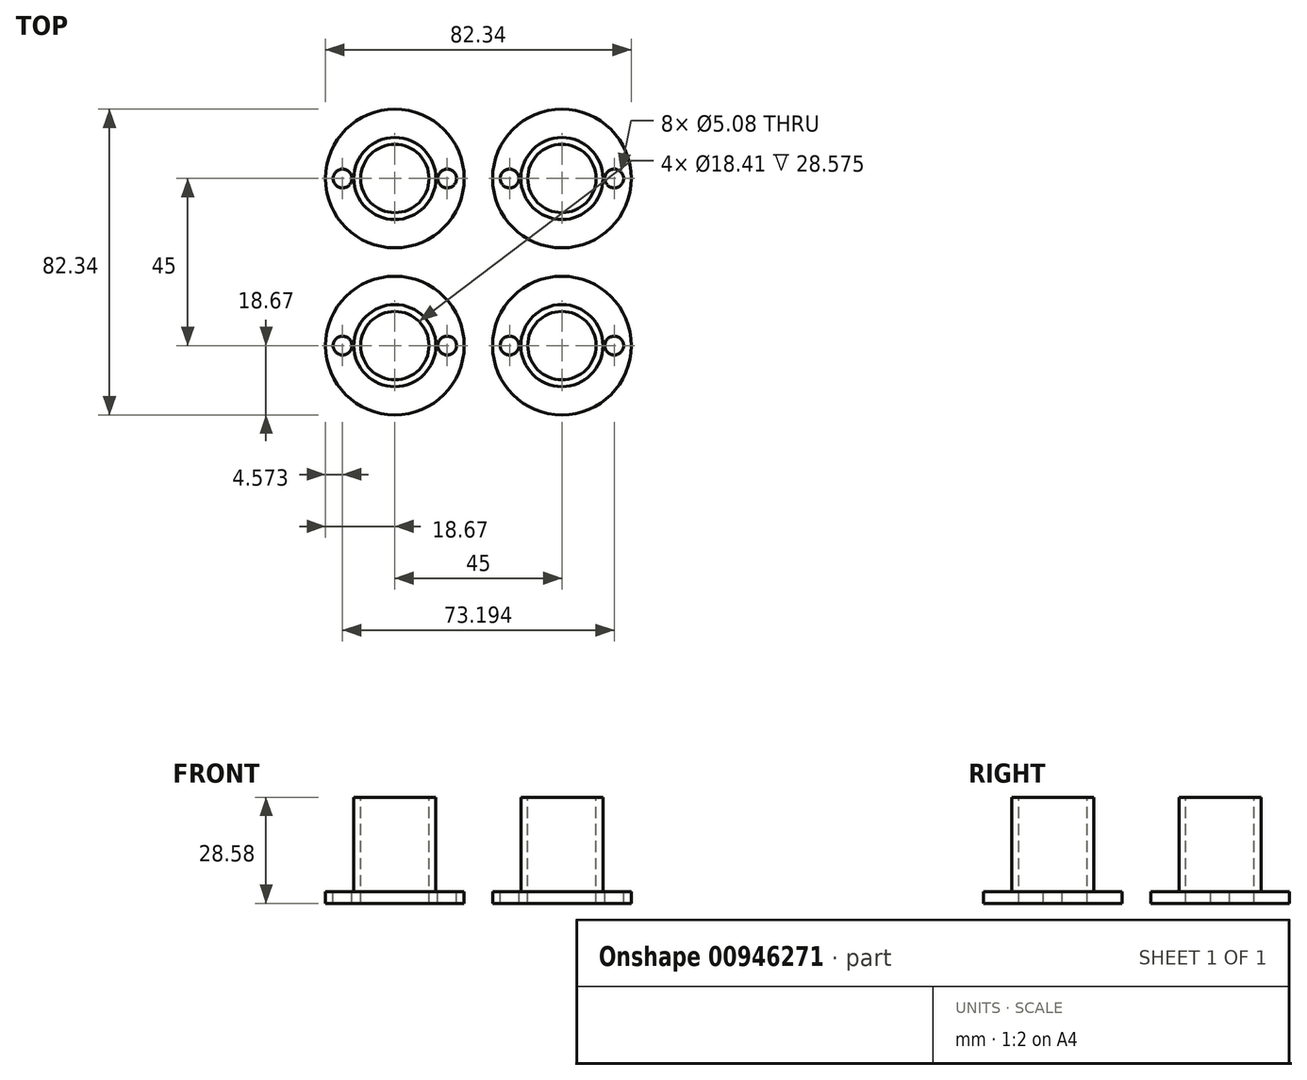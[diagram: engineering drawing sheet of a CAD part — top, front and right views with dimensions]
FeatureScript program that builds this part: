
annotation { "Feature Type Name" : "Feature", "Feature Type Description" : "" }
export const myFeature = defineFeature(function(context is Context, id is Id, definition is map)
    precondition{}
    {
        {
            var Q0;
            Q0=qCreatedBy(makeId("Top.planeOp"),FACE);
            var sketch = newSketch(context, id + "F0", { "sketchPlane" : qUnion([Q0])});
            skCircle(sketch, "E0", {"center": v(0, 0) * mm, "radius": 9.2 * mm});
            skCircle(sketch, "E1.0", {"center": v(0, 0) * mm, "radius": 11.05 * mm});
            skCircle(sketch, "E2.0", {"center": v(0, 0) * mm, "radius": 18.67 * mm});
            skCircle(sketch, "E3.0", {"center": v(0, 0) * mm, "radius": 14.1 * mm});
            skCircle(sketch, "E4", {"center": v(-14.1, 0) * mm, "radius": 2.54 * mm});
            skCircle(sketch, "E5", {"center": v(14.1, 0) * mm, "radius": 2.54 * mm});
            skSolve(sketch);
        }
        {
            var Q0;
            Q0=makeQuery(id+"F0.imprint","IMPRINT",FACE,{"disambiguationData":[TD([[makeQuery(id+"F0.imprint","IMPRINT",EDGE,{"derivedFrom":sQuery(id+"F0.wireOp",EDGE,"E2.0")}),1.0]])]});
            var Q1;
            Q1=makeQuery(id+"F0.imprint","IMPRINT",FACE,{"disambiguationData":[TD([[makeQuery(id+"F0.imprint","IMPRINT",EDGE,{"derivedFrom":sQuery(id+"F0.wireOp",EDGE,"E1.0")}),-1.0]])]});
            var Q2;
            Q2=makeQuery(id+"F0.imprint","IMPRINT",FACE,{"disambiguationData":[TD([[makeQuery(id+"F0.imprint","IMPRINT",EDGE,{"derivedFrom":sQuery(id+"F0.wireOp",EDGE,"E0")}),-1.0]])]});
            extrude(context, id + "F1", {"entities" : qUnion([Q0, Q1, Q2]), "oppositeDirection" : true, "depth" : 3.17 * mm, "offsetDistance" : 25.4 * mm});
        }
        {
            var Q0;
            Q0=makeQuery(id+"F0.imprint","IMPRINT",FACE,{"disambiguationData":[TD([[makeQuery(id+"F0.imprint","IMPRINT",EDGE,{"derivedFrom":sQuery(id+"F0.wireOp",EDGE,"E0")}),-1.0]])]});
            extrude(context, id + "F2", {"entities" : qUnion([Q0]), "operationType" : NewBodyOperationType.ADD, "depth" : 25.4 * mm, "offsetDistance" : 25.4 * mm});
        }
        {
            var Q0;
            Q0=makeQuery(id+"F1.opExtrude","SWEPT_BODY",BODY,{"disambiguationData":[OSD([sQuery(id+"F0.wireOp",EDGE,"E0"),sQuery(id+"F0.wireOp",EDGE,"E2.0"),sQuery(id+"F0.wireOp",EDGE,"E4"),sQuery(id+"F0.wireOp",EDGE,"E5")])]});
            transform(context, id + "F3", {"entities" : qUnion([Q0]), "transformType" : TransformType.TRANSLATION_3D, "dx" : 45 * mm, "dy" : 0 * mm, "dz" : 0 * mm, "makeCopy" : true});
        }
        {
            var Q0;
            Q0=makeQuery(id+"F1.opExtrude","SWEPT_BODY",BODY,{"disambiguationData":[OSD([sQuery(id+"F0.wireOp",EDGE,"E0"),sQuery(id+"F0.wireOp",EDGE,"E2.0"),sQuery(id+"F0.wireOp",EDGE,"E4"),sQuery(id+"F0.wireOp",EDGE,"E5")])]});
            var Q1;
            Q1=makeQuery(id+"F3.opPattern","COPY",BODY,{"derivedFrom":makeQuery(id+"F1.opExtrude","SWEPT_BODY",BODY,{"disambiguationData":[OSD([sQuery(id+"F0.wireOp",EDGE,"E0"),sQuery(id+"F0.wireOp",EDGE,"E2.0"),sQuery(id+"F0.wireOp",EDGE,"E4"),sQuery(id+"F0.wireOp",EDGE,"E5")])]}),"instanceName":"1"});
            transform(context, id + "F4", {"entities" : qUnion([Q0, Q1]), "transformType" : TransformType.TRANSLATION_3D, "dx" : 0 * mm, "dy" : 45 * mm, "dz" : 0 * mm, "makeCopy" : true});
        }
    });
